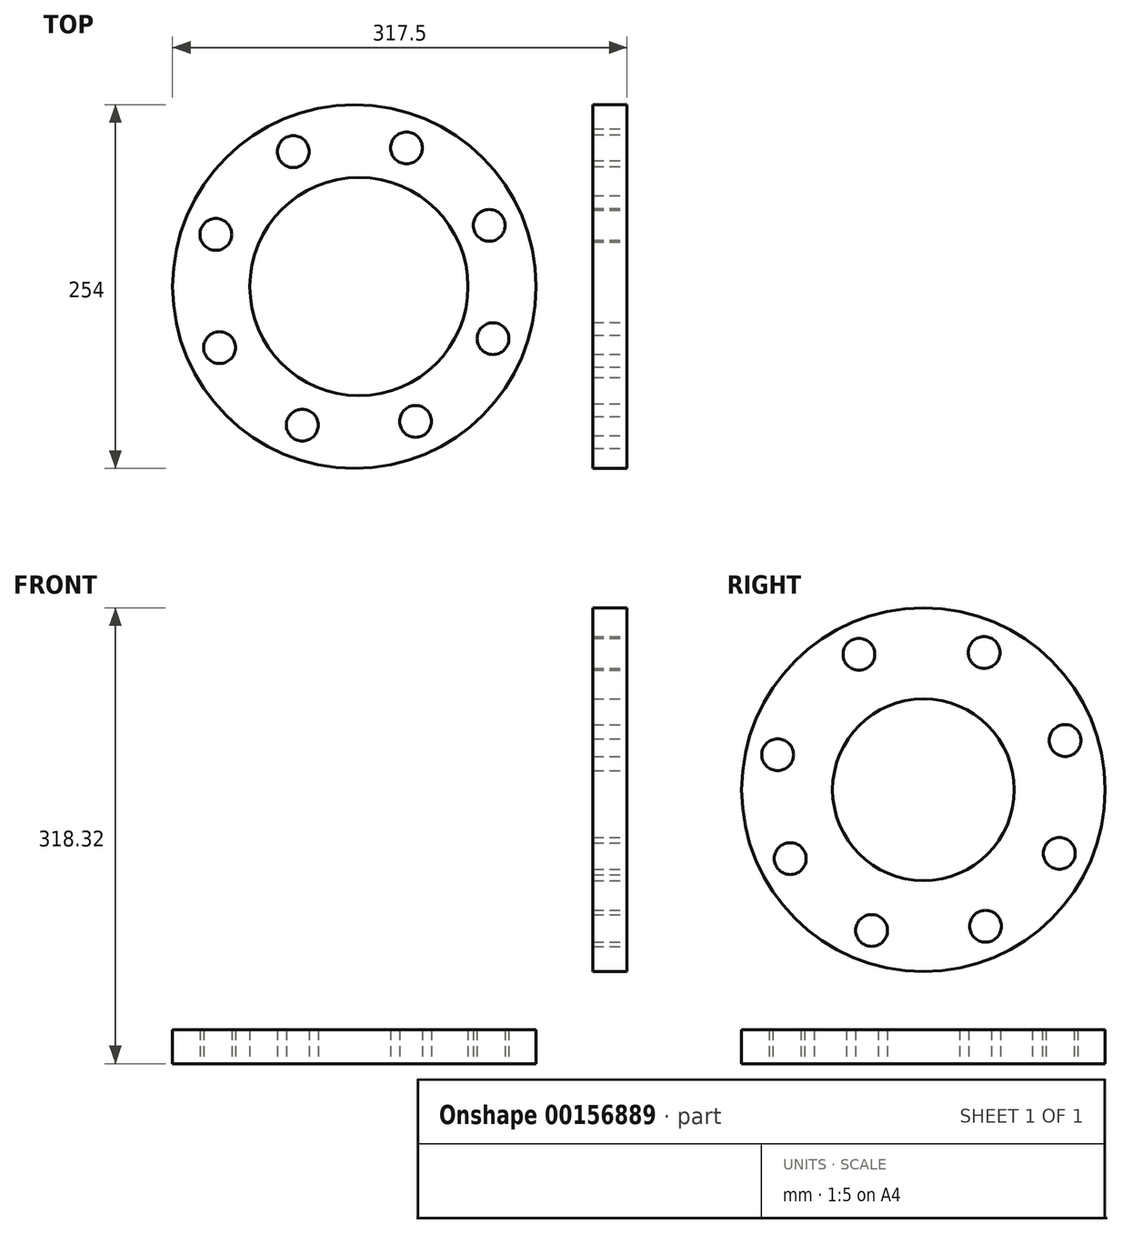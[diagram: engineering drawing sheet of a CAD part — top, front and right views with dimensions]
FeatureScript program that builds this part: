
annotation { "Feature Type Name" : "Feature", "Feature Type Description" : "" }
export const myFeature = defineFeature(function(context is Context, id is Id, definition is map)
    precondition{}
    {
        {
            var Q0;
            Q0=qCreatedBy(makeId("Top.planeOp"),FACE);
            var sketch = newSketch(context, id + "F0", { "sketchPlane" : qUnion([Q0])});
            skCircle(sketch, "E0", {"center": v(0, 0) * mm, "radius": 63.5 * mm});
            skCircle(sketch, "E1", {"center": v(3.17, 0) * mm, "radius": 76.2 * mm});
            skCircle(sketch, "E2", {"center": v(0, 0) * mm, "radius": 127 * mm});
            skCircle(sketch, "E3", {"center": v(3.17, 0) * mm, "radius": 104.78 * mm});
            skCircle(sketch, "E4", {"center": v(-42.71, 94.2) * mm, "radius": 11.11 * mm});
            skCircle(sketch, "E5.1.0", {"center": v(-96.8, 36.4) * mm, "radius": 11.11 * mm});
            skCircle(sketch, "E5.2.0", {"center": v(-94.2, -42.71) * mm, "radius": 11.11 * mm});
            skCircle(sketch, "E6.1.3.0", {"center": v(-36.4, -96.8) * mm, "radius": 11.11 * mm});
            skCircle(sketch, "E6.1.4.0", {"center": v(42.71, -94.2) * mm, "radius": 11.11 * mm});
            skCircle(sketch, "E6.1.5.0", {"center": v(96.8, -36.4) * mm, "radius": 11.11 * mm});
            skCircle(sketch, "E6.1.6.0", {"center": v(94.2, 42.71) * mm, "radius": 11.11 * mm});
            skCircle(sketch, "E6.1.7.0", {"center": v(36.4, 96.8) * mm, "radius": 11.11 * mm});
            skSolve(sketch);
        }
        {
            var Q0;
            Q0=makeQuery(id+"F0.imprint","IMPRINT",FACE,{"disambiguationData":[TD([[makeQuery(id+"F0.imprint","IMPRINT",EDGE,{"derivedFrom":sQuery(id+"F0.wireOp",EDGE,"E2")}),1.0]])]});
            var Q1;
            Q1=makeQuery(id+"F0.imprint","IMPRINT",FACE,{"disambiguationData":[TD([[makeQuery(id+"F0.imprint","IMPRINT",EDGE,{"derivedFrom":sQuery(id+"F0.wireOp",EDGE,"E1")}),-1.0]])]});
            extrude(context, id + "F1", {"entities" : qUnion([Q0, Q1]), "depth" : 23.8 * mm});
        }
        {
            var Q0;
            Q0=qCreatedBy(makeId("Front.planeOp"),FACE);
            var sketch = newSketch(context, id + "F2", { "sketchPlane" : qUnion([Q0])});
            skLineSegment(sketch, "E7.top", {"start": v(166.69, 190.5) * mm, "end": v(190.5, 190.5) * mm});
            skLineSegment(sketch, "E7.left", {"start": v(0, 0) * mm, "end": v(0, 23.81) * mm});
            skLineSegment(sketch, "E7.right", {"start": v(190.5, 0) * mm, "end": v(190.5, 190.5) * mm});
            skPoint(sketch, "E8.visualSharp", {"position": v(0, 190.5) * mm});
            skArc(sketch, "E8.filletArc", {"start": v(166.69, 190.5) * mm, "mid": v(48.82, 141.68) * mm, "end": v(0, 23.81) * mm});
            skSolve(sketch);
        }
        {
            var Q0;
            Q0=qCreatedBy(makeId("Right.planeOp"),FACE);
            cPlane(context, id + "F3", {"entities" : qUnion([Q0]), "cplaneType" : CPlaneType.OFFSET, "offset" : 190.5 * mm, "width" : 152.4 * mm, "height" : 152.4 * mm});
        }
        {
            var Q0;
            Q0=qCreatedBy(id+"F3.planeOp",FACE);
            var sketch = newSketch(context, id + "F4", { "sketchPlane" : qUnion([Q0])});
            skCircle(sketch, "E9", {"center": v(0, 191.32) * mm, "radius": 127 * mm});
            skCircle(sketch, "E10", {"center": v(-36.25, 93.01) * mm, "radius": 11.11 * mm});
            skCircle(sketch, "E11", {"center": v(-93.08, 143.21) * mm, "radius": 11.11 * mm});
            skCircle(sketch, "E12", {"center": v(-101.88, 215.76) * mm, "radius": 11.11 * mm});
            skCircle(sketch, "E13", {"center": v(-45.06, 285.9) * mm, "radius": 11.11 * mm});
            skCircle(sketch, "E14", {"center": v(42.36, 287.15) * mm, "radius": 11.11 * mm});
            skCircle(sketch, "E15", {"center": v(98.98, 225.7) * mm, "radius": 11.11 * mm});
            skCircle(sketch, "E16", {"center": v(94.89, 146.89) * mm, "radius": 11.11 * mm});
            skCircle(sketch, "E17", {"center": v(43.35, 95.93) * mm, "radius": 11.11 * mm});
            skCircle(sketch, "E18", {"center": v(0, 191.32) * mm, "radius": 63.5 * mm});
            skSolve(sketch);
        }
        {
            var Q0;
            Q0=makeQuery(id+"F4.imprint","IMPRINT",FACE,{"disambiguationData":[TD([[makeQuery(id+"F4.imprint","IMPRINT",EDGE,{"derivedFrom":sQuery(id+"F4.wireOp",EDGE,"E9")}),1.0]])]});
            extrude(context, id + "F5", {"entities" : qUnion([Q0]), "oppositeDirection" : true, "depth" : 23.8 * mm});
        }
        {
            var Q0;
            Q0=sQuery(id+"F0.wireOp",EDGE,"E1");
            extrude(context, id + "F6", {"bodyType" : ToolBodyType.SURFACE, "surfaceEntities" : qUnion([Q0]), "depth" : 25.4 * mm});
        }
    });
